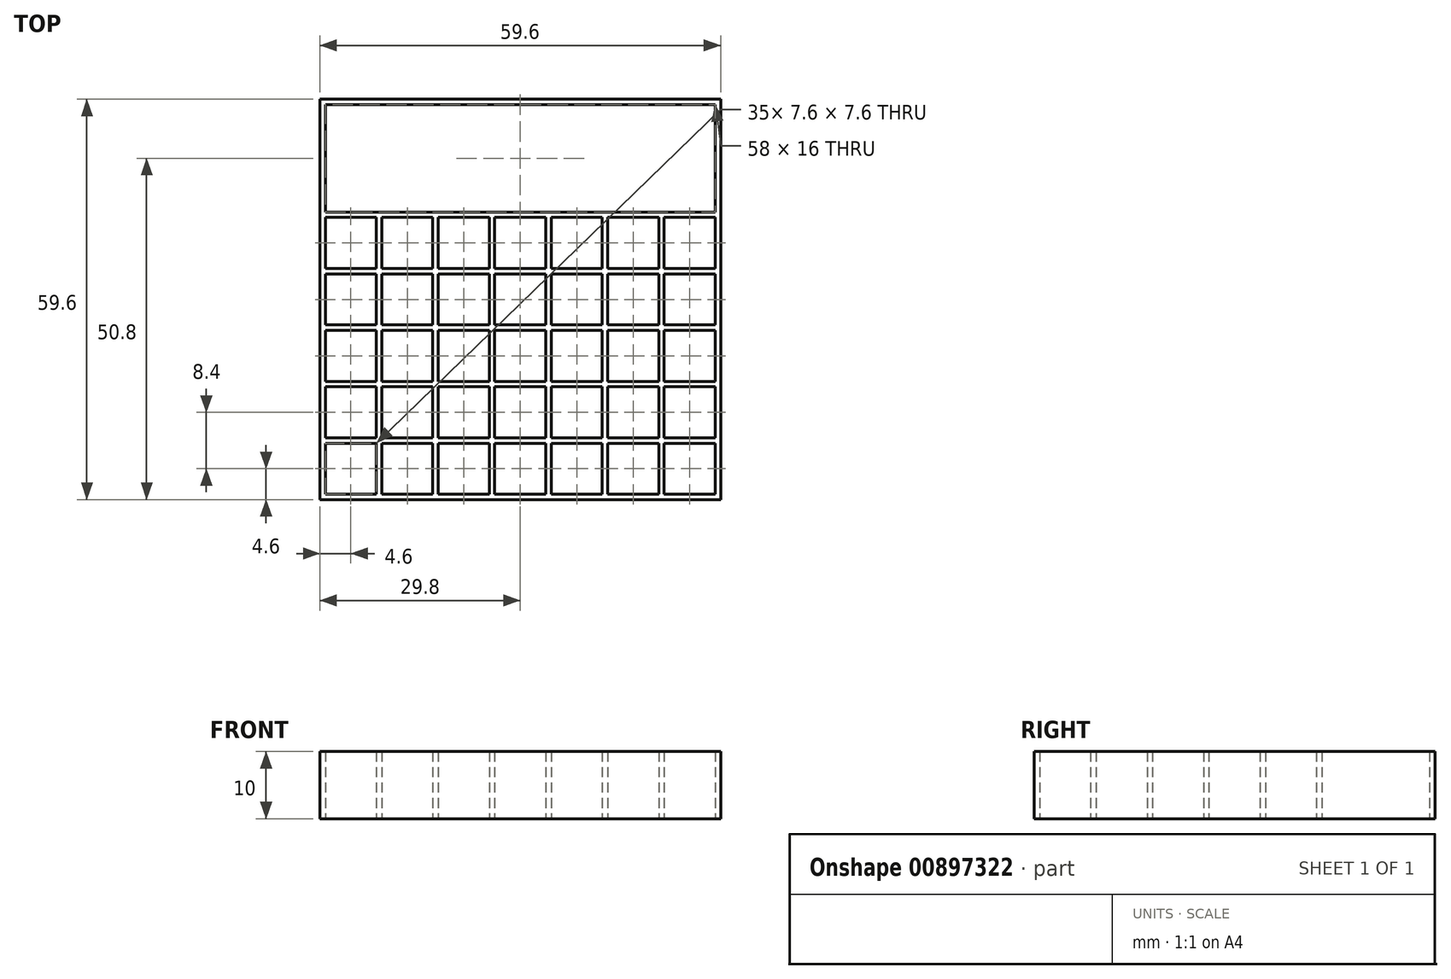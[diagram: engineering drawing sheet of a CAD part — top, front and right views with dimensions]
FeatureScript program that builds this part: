
annotation { "Feature Type Name" : "Feature", "Feature Type Description" : "" }
export const myFeature = defineFeature(function(context is Context, id is Id, definition is map)
    precondition{}
    {
        {
            var Q0;
            Q0=qCreatedBy(makeId("Top.planeOp"),FACE);
            var sketch = newSketch(context, id + "F0", { "sketchPlane" : qUnion([Q0])});
            skLineSegment(sketch, "E0.bottom", {"start": v(0, 29.8) * mm, "end": v(-29.8, 29.8) * mm});
            skLineSegment(sketch, "E1", {"start": v(-29.8, 29.8) * mm, "end": v(-29.8, 0) * mm});
            skLineSegment(sketch, "E2.2.0.1", {"start": v(-29, 12.2) * mm, "end": v(-21.4, 12.2) * mm});
            skLineSegment(sketch, "E2.2.0.4", {"start": v(-21.4, 12.2) * mm, "end": v(-21.4, 4.6) * mm});
            skLineSegment(sketch, "E2.2.0.7", {"start": v(-29, 12.2) * mm, "end": v(-29, 4.6) * mm});
            skLineSegment(sketch, "E2.2.0.15", {"start": v(-29, 4.6) * mm, "end": v(-21.4, 4.6) * mm});
            skLineSegment(sketch, "E3.MirrorCS", {"start": v(-29.8, -29.8) * mm, "end": v(-29.8, 0) * mm});
            skLineSegment(sketch, "E4.MirrorCS", {"start": v(0, -29.8) * mm, "end": v(-29.8, -29.8) * mm});
            skLineSegment(sketch, "E5", {"start": v(-29, 13) * mm, "end": v(0, 13) * mm});
            skLineSegment(sketch, "E6", {"start": v(-29, 13) * mm, "end": v(-29, 29) * mm});
            skLineSegment(sketch, "E7", {"start": v(-29, 29) * mm, "end": v(0, 29) * mm});
            skLineSegment(sketch, "E8.2.0.1", {"start": v(-20.6, 12.2) * mm, "end": v(-13, 12.2) * mm});
            skLineSegment(sketch, "E8.2.0.4", {"start": v(-13, 12.2) * mm, "end": v(-13, 4.6) * mm});
            skLineSegment(sketch, "E8.2.0.7", {"start": v(-20.6, 12.2) * mm, "end": v(-20.6, 4.6) * mm});
            skLineSegment(sketch, "E8.2.0.15", {"start": v(-20.6, 4.6) * mm, "end": v(-13, 4.6) * mm});
            skLineSegment(sketch, "E9.2.0.1", {"start": v(-12.2, 12.2) * mm, "end": v(-4.6, 12.2) * mm});
            skLineSegment(sketch, "E9.2.0.4", {"start": v(-4.6, 12.2) * mm, "end": v(-4.6, 4.6) * mm});
            skLineSegment(sketch, "E9.2.0.7", {"start": v(-12.2, 12.2) * mm, "end": v(-12.2, 4.6) * mm});
            skLineSegment(sketch, "E9.2.0.15", {"start": v(-12.2, 4.6) * mm, "end": v(-4.6, 4.6) * mm});
            skLineSegment(sketch, "E10.2.0.1", {"start": v(-3.8, 12.2) * mm, "end": v(0, 12.2) * mm});
            skLineSegment(sketch, "E10.2.0.7", {"start": v(-3.8, 12.2) * mm, "end": v(-3.8, 4.6) * mm});
            skLineSegment(sketch, "E10.2.0.15", {"start": v(-3.8, 4.6) * mm, "end": v(0, 4.6) * mm});
            skLineSegment(sketch, "E11.1.0.0", {"start": v(-20.6, 3.8) * mm, "end": v(-13, 3.8) * mm});
            skLineSegment(sketch, "E11.1.0.1", {"start": v(-29, -3.8) * mm, "end": v(-21.4, -3.8) * mm});
            skLineSegment(sketch, "E11.1.0.2", {"start": v(-21.4, 3.8) * mm, "end": v(-21.4, -3.8) * mm});
            skLineSegment(sketch, "E11.1.0.3", {"start": v(-12.2, 3.8) * mm, "end": v(-12.2, -3.8) * mm});
            skLineSegment(sketch, "E11.1.0.4", {"start": v(-4.6, 3.8) * mm, "end": v(-4.6, -3.8) * mm});
            skLineSegment(sketch, "E11.1.0.5", {"start": v(-29, 3.8) * mm, "end": v(-29, -3.8) * mm});
            skLineSegment(sketch, "E11.1.0.6", {"start": v(-3.8, -3.8) * mm, "end": v(0, -3.8) * mm});
            skLineSegment(sketch, "E11.1.0.7", {"start": v(-12.2, -3.8) * mm, "end": v(-4.6, -3.8) * mm});
            skLineSegment(sketch, "E11.1.0.8", {"start": v(-20.6, -3.8) * mm, "end": v(-13, -3.8) * mm});
            skLineSegment(sketch, "E11.1.0.9", {"start": v(-3.8, 3.8) * mm, "end": v(0, 3.8) * mm});
            skLineSegment(sketch, "E11.1.0.10", {"start": v(-20.6, 3.8) * mm, "end": v(-20.6, -3.8) * mm});
            skLineSegment(sketch, "E11.1.0.11", {"start": v(-29, 3.8) * mm, "end": v(-21.4, 3.8) * mm});
            skLineSegment(sketch, "E11.1.0.12", {"start": v(-12.2, 3.8) * mm, "end": v(-4.6, 3.8) * mm});
            skLineSegment(sketch, "E11.1.0.13", {"start": v(-3.8, 3.8) * mm, "end": v(-3.8, -3.8) * mm});
            skLineSegment(sketch, "E11.1.0.14", {"start": v(-13, 3.8) * mm, "end": v(-13, -3.8) * mm});
            skLineSegment(sketch, "E11.2.0.0", {"start": v(-20.6, -4.6) * mm, "end": v(-13, -4.6) * mm});
            skLineSegment(sketch, "E11.2.0.1", {"start": v(-29, -12.2) * mm, "end": v(-21.4, -12.2) * mm});
            skLineSegment(sketch, "E11.2.0.2", {"start": v(-21.4, -4.6) * mm, "end": v(-21.4, -12.2) * mm});
            skLineSegment(sketch, "E11.2.0.3", {"start": v(-12.2, -4.6) * mm, "end": v(-12.2, -12.2) * mm});
            skLineSegment(sketch, "E11.2.0.4", {"start": v(-4.6, -4.6) * mm, "end": v(-4.6, -12.2) * mm});
            skLineSegment(sketch, "E11.2.0.5", {"start": v(-29, -4.6) * mm, "end": v(-29, -12.2) * mm});
            skLineSegment(sketch, "E11.2.0.6", {"start": v(-3.8, -12.2) * mm, "end": v(0, -12.2) * mm});
            skLineSegment(sketch, "E11.2.0.7", {"start": v(-12.2, -12.2) * mm, "end": v(-4.6, -12.2) * mm});
            skLineSegment(sketch, "E11.2.0.8", {"start": v(-20.6, -12.2) * mm, "end": v(-13, -12.2) * mm});
            skLineSegment(sketch, "E11.2.0.9", {"start": v(-3.8, -4.6) * mm, "end": v(0, -4.6) * mm});
            skLineSegment(sketch, "E11.2.0.10", {"start": v(-20.6, -4.6) * mm, "end": v(-20.6, -12.2) * mm});
            skLineSegment(sketch, "E11.2.0.11", {"start": v(-29, -4.6) * mm, "end": v(-21.4, -4.6) * mm});
            skLineSegment(sketch, "E11.2.0.12", {"start": v(-12.2, -4.6) * mm, "end": v(-4.6, -4.6) * mm});
            skLineSegment(sketch, "E11.2.0.13", {"start": v(-3.8, -4.6) * mm, "end": v(-3.8, -12.2) * mm});
            skLineSegment(sketch, "E11.2.0.14", {"start": v(-13, -4.6) * mm, "end": v(-13, -12.2) * mm});
            skLineSegment(sketch, "E11.3.0.0", {"start": v(-20.6, -13) * mm, "end": v(-13, -13) * mm});
            skLineSegment(sketch, "E11.3.0.1", {"start": v(-29, -20.6) * mm, "end": v(-21.4, -20.6) * mm});
            skLineSegment(sketch, "E11.3.0.2", {"start": v(-21.4, -13) * mm, "end": v(-21.4, -20.6) * mm});
            skLineSegment(sketch, "E11.3.0.3", {"start": v(-12.2, -13) * mm, "end": v(-12.2, -20.6) * mm});
            skLineSegment(sketch, "E11.3.0.4", {"start": v(-4.6, -13) * mm, "end": v(-4.6, -20.6) * mm});
            skLineSegment(sketch, "E11.3.0.5", {"start": v(-29, -13) * mm, "end": v(-29, -20.6) * mm});
            skLineSegment(sketch, "E11.3.0.6", {"start": v(-3.8, -20.6) * mm, "end": v(0, -20.6) * mm});
            skLineSegment(sketch, "E11.3.0.7", {"start": v(-12.2, -20.6) * mm, "end": v(-4.6, -20.6) * mm});
            skLineSegment(sketch, "E11.3.0.8", {"start": v(-20.6, -20.6) * mm, "end": v(-13, -20.6) * mm});
            skLineSegment(sketch, "E11.3.0.9", {"start": v(-3.8, -13) * mm, "end": v(0, -13) * mm});
            skLineSegment(sketch, "E11.3.0.10", {"start": v(-20.6, -13) * mm, "end": v(-20.6, -20.6) * mm});
            skLineSegment(sketch, "E11.3.0.11", {"start": v(-29, -13) * mm, "end": v(-21.4, -13) * mm});
            skLineSegment(sketch, "E11.3.0.12", {"start": v(-12.2, -13) * mm, "end": v(-4.6, -13) * mm});
            skLineSegment(sketch, "E11.3.0.13", {"start": v(-3.8, -13) * mm, "end": v(-3.8, -20.6) * mm});
            skLineSegment(sketch, "E11.3.0.14", {"start": v(-13, -13) * mm, "end": v(-13, -20.6) * mm});
            skLineSegment(sketch, "E11.4.0.0", {"start": v(-20.6, -21.4) * mm, "end": v(-13, -21.4) * mm});
            skLineSegment(sketch, "E11.4.0.1", {"start": v(-29, -29) * mm, "end": v(-21.4, -29) * mm});
            skLineSegment(sketch, "E11.4.0.2", {"start": v(-21.4, -21.4) * mm, "end": v(-21.4, -29) * mm});
            skLineSegment(sketch, "E11.4.0.3", {"start": v(-12.2, -21.4) * mm, "end": v(-12.2, -29) * mm});
            skLineSegment(sketch, "E11.4.0.4", {"start": v(-4.6, -21.4) * mm, "end": v(-4.6, -29) * mm});
            skLineSegment(sketch, "E11.4.0.5", {"start": v(-29, -21.4) * mm, "end": v(-29, -29) * mm});
            skLineSegment(sketch, "E11.4.0.6", {"start": v(-3.8, -29) * mm, "end": v(0, -29) * mm});
            skLineSegment(sketch, "E11.4.0.7", {"start": v(-12.2, -29) * mm, "end": v(-4.6, -29) * mm});
            skLineSegment(sketch, "E11.4.0.8", {"start": v(-20.6, -29) * mm, "end": v(-13, -29) * mm});
            skLineSegment(sketch, "E11.4.0.9", {"start": v(-3.8, -21.4) * mm, "end": v(0, -21.4) * mm});
            skLineSegment(sketch, "E11.4.0.10", {"start": v(-20.6, -21.4) * mm, "end": v(-20.6, -29) * mm});
            skLineSegment(sketch, "E11.4.0.11", {"start": v(-29, -21.4) * mm, "end": v(-21.4, -21.4) * mm});
            skLineSegment(sketch, "E11.4.0.12", {"start": v(-12.2, -21.4) * mm, "end": v(-4.6, -21.4) * mm});
            skLineSegment(sketch, "E11.4.0.13", {"start": v(-3.8, -21.4) * mm, "end": v(-3.8, -29) * mm});
            skLineSegment(sketch, "E11.4.0.14", {"start": v(-13, -21.4) * mm, "end": v(-13, -29) * mm});
            skLineSegment(sketch, "E11.direction1", {"start": v(-29, 4.6) * mm, "end": v(-29, -3.8) * mm, "construction": true});
            skLineSegment(sketch, "E12.MirrorCS", {"start": v(3.8, 12.2) * mm, "end": v(3.8, 4.6) * mm});
            skLineSegment(sketch, "E13.MirrorCS", {"start": v(3.8, 12.2) * mm, "end": v(0, 12.2) * mm});
            skLineSegment(sketch, "E14.MirrorCS", {"start": v(12.2, 12.2) * mm, "end": v(12.2, 4.6) * mm});
            skLineSegment(sketch, "E15.MirrorCS", {"start": v(29, 3.8) * mm, "end": v(29, -3.8) * mm});
            skLineSegment(sketch, "E16.MirrorCS", {"start": v(20.6, 12.2) * mm, "end": v(20.6, 4.6) * mm});
            skLineSegment(sketch, "E17.MirrorCS", {"start": v(20.6, 3.8) * mm, "end": v(13, 3.8) * mm});
            skLineSegment(sketch, "E18.MirrorCS", {"start": v(29.8, -29.8) * mm, "end": v(29.8, 0) * mm});
            skLineSegment(sketch, "E19.MirrorCS", {"start": v(29.8, 29.8) * mm, "end": v(29.8, 0) * mm});
            skLineSegment(sketch, "E20.MirrorCS", {"start": v(20.6, -21.4) * mm, "end": v(20.6, -29) * mm});
            skLineSegment(sketch, "E21.MirrorCS", {"start": v(12.2, -4.6) * mm, "end": v(4.6, -4.6) * mm});
            skLineSegment(sketch, "E22.MirrorCS", {"start": v(20.6, -21.4) * mm, "end": v(13, -21.4) * mm});
            skLineSegment(sketch, "E23.MirrorCS", {"start": v(12.2, -13) * mm, "end": v(4.6, -13) * mm});
            skLineSegment(sketch, "E24.MirrorCS", {"start": v(12.2, 3.8) * mm, "end": v(12.2, -3.8) * mm});
            skLineSegment(sketch, "E25.MirrorCS", {"start": v(29, -21.4) * mm, "end": v(29, -29) * mm});
            skLineSegment(sketch, "E26.MirrorCS", {"start": v(20.6, -3.8) * mm, "end": v(13, -3.8) * mm});
            skLineSegment(sketch, "E27.MirrorCS", {"start": v(29, -4.6) * mm, "end": v(21.4, -4.6) * mm});
            skLineSegment(sketch, "E28.MirrorCS", {"start": v(21.4, -13) * mm, "end": v(21.4, -20.6) * mm});
            skLineSegment(sketch, "E29.MirrorCS", {"start": v(3.8, -13) * mm, "end": v(3.8, -20.6) * mm});
            skLineSegment(sketch, "E30.MirrorCS", {"start": v(29, 4.6) * mm, "end": v(21.4, 4.6) * mm});
            skLineSegment(sketch, "E31.MirrorCS", {"start": v(0, -29.8) * mm, "end": v(29.8, -29.8) * mm});
            skLineSegment(sketch, "E32.MirrorCS", {"start": v(20.6, -20.6) * mm, "end": v(13, -20.6) * mm});
            skLineSegment(sketch, "E33.MirrorCS", {"start": v(3.8, -12.2) * mm, "end": v(0, -12.2) * mm});
            skLineSegment(sketch, "E34.MirrorCS", {"start": v(12.2, -21.4) * mm, "end": v(4.6, -21.4) * mm});
            skLineSegment(sketch, "E35.MirrorCS", {"start": v(3.8, -13) * mm, "end": v(0, -13) * mm});
            skLineSegment(sketch, "E36.MirrorCS", {"start": v(4.6, -21.4) * mm, "end": v(4.6, -29) * mm});
            skLineSegment(sketch, "E37.MirrorCS", {"start": v(20.6, -29) * mm, "end": v(13, -29) * mm});
            skLineSegment(sketch, "E38.MirrorCS", {"start": v(20.6, 12.2) * mm, "end": v(13, 12.2) * mm});
            skLineSegment(sketch, "E39.MirrorCS", {"start": v(29, 13) * mm, "end": v(29, 29) * mm});
            skLineSegment(sketch, "E40.MirrorCS", {"start": v(13, -21.4) * mm, "end": v(13, -29) * mm});
            skLineSegment(sketch, "E41.MirrorCS", {"start": v(12.2, 4.6) * mm, "end": v(4.6, 4.6) * mm});
            skLineSegment(sketch, "E42.MirrorCS", {"start": v(29, -3.8) * mm, "end": v(21.4, -3.8) * mm});
            skLineSegment(sketch, "E43.MirrorCS", {"start": v(29, -21.4) * mm, "end": v(21.4, -21.4) * mm});
            skLineSegment(sketch, "E44.MirrorCS", {"start": v(20.6, -13) * mm, "end": v(13, -13) * mm});
            skLineSegment(sketch, "E45.MirrorCS", {"start": v(29, 3.8) * mm, "end": v(21.4, 3.8) * mm});
            skLineSegment(sketch, "E46.MirrorCS", {"start": v(29, -4.6) * mm, "end": v(29, -12.2) * mm});
            skLineSegment(sketch, "E47.MirrorCS", {"start": v(13, -4.6) * mm, "end": v(13, -12.2) * mm});
            skLineSegment(sketch, "E48.MirrorCS", {"start": v(3.8, -21.4) * mm, "end": v(0, -21.4) * mm});
            skLineSegment(sketch, "E49.MirrorCS", {"start": v(3.8, 3.8) * mm, "end": v(3.8, -3.8) * mm});
            skLineSegment(sketch, "E50.MirrorCS", {"start": v(20.6, -12.2) * mm, "end": v(13, -12.2) * mm});
            skLineSegment(sketch, "E51.MirrorCS", {"start": v(12.2, -3.8) * mm, "end": v(4.6, -3.8) * mm});
            skLineSegment(sketch, "E52.MirrorCS", {"start": v(21.4, -21.4) * mm, "end": v(21.4, -29) * mm});
            skLineSegment(sketch, "E53.MirrorCS", {"start": v(12.2, -20.6) * mm, "end": v(4.6, -20.6) * mm});
            skLineSegment(sketch, "E54.MirrorCS", {"start": v(13, 12.2) * mm, "end": v(13, 4.6) * mm});
            skLineSegment(sketch, "E55.MirrorCS", {"start": v(3.8, -4.6) * mm, "end": v(0, -4.6) * mm});
            skLineSegment(sketch, "E56.MirrorCS", {"start": v(12.2, 12.2) * mm, "end": v(4.6, 12.2) * mm});
            skLineSegment(sketch, "E57.MirrorCS", {"start": v(29, 12.2) * mm, "end": v(29, 4.6) * mm});
            skLineSegment(sketch, "E58.MirrorCS", {"start": v(12.2, -4.6) * mm, "end": v(12.2, -12.2) * mm});
            skLineSegment(sketch, "E59.MirrorCS", {"start": v(29, -12.2) * mm, "end": v(21.4, -12.2) * mm});
            skLineSegment(sketch, "E60.MirrorCS", {"start": v(13, -13) * mm, "end": v(13, -20.6) * mm});
            skLineSegment(sketch, "E61.MirrorCS", {"start": v(3.8, -21.4) * mm, "end": v(3.8, -29) * mm});
            skLineSegment(sketch, "E62.MirrorCS", {"start": v(12.2, -29) * mm, "end": v(4.6, -29) * mm});
            skLineSegment(sketch, "E63.MirrorCS", {"start": v(21.4, -4.6) * mm, "end": v(21.4, -12.2) * mm});
            skLineSegment(sketch, "E64.MirrorCS", {"start": v(0, 29.8) * mm, "end": v(29.8, 29.8) * mm});
            skLineSegment(sketch, "E65.MirrorCS", {"start": v(21.4, 3.8) * mm, "end": v(21.4, -3.8) * mm});
            skLineSegment(sketch, "E66.MirrorCS", {"start": v(29, 29) * mm, "end": v(0, 29) * mm});
            skLineSegment(sketch, "E67.MirrorCS", {"start": v(29, -13) * mm, "end": v(29, -20.6) * mm});
            skLineSegment(sketch, "E68.MirrorCS", {"start": v(20.6, -4.6) * mm, "end": v(13, -4.6) * mm});
            skLineSegment(sketch, "E69.MirrorCS", {"start": v(4.6, -4.6) * mm, "end": v(4.6, -12.2) * mm});
            skLineSegment(sketch, "E70.MirrorCS", {"start": v(29, -13) * mm, "end": v(21.4, -13) * mm});
            skLineSegment(sketch, "E71.MirrorCS", {"start": v(12.2, 3.8) * mm, "end": v(4.6, 3.8) * mm});
            skLineSegment(sketch, "E72.MirrorCS", {"start": v(3.8, 4.6) * mm, "end": v(0, 4.6) * mm});
            skLineSegment(sketch, "E73.MirrorCS", {"start": v(3.8, 3.8) * mm, "end": v(0, 3.8) * mm});
            skLineSegment(sketch, "E74.MirrorCS", {"start": v(29, 13) * mm, "end": v(0, 13) * mm});
            skLineSegment(sketch, "E75.MirrorCS", {"start": v(4.6, -13) * mm, "end": v(4.6, -20.6) * mm});
            skLineSegment(sketch, "E76.MirrorCS", {"start": v(3.8, -20.6) * mm, "end": v(0, -20.6) * mm});
            skLineSegment(sketch, "E77.MirrorCS", {"start": v(20.6, 4.6) * mm, "end": v(13, 4.6) * mm});
            skLineSegment(sketch, "E78.MirrorCS", {"start": v(12.2, -12.2) * mm, "end": v(4.6, -12.2) * mm});
            skLineSegment(sketch, "E79.MirrorCS", {"start": v(12.2, -21.4) * mm, "end": v(12.2, -29) * mm});
            skLineSegment(sketch, "E80.MirrorCS", {"start": v(20.6, -13) * mm, "end": v(20.6, -20.6) * mm});
            skLineSegment(sketch, "E81.MirrorCS", {"start": v(21.4, 12.2) * mm, "end": v(21.4, 4.6) * mm});
            skLineSegment(sketch, "E82.MirrorCS", {"start": v(4.6, 3.8) * mm, "end": v(4.6, -3.8) * mm});
            skLineSegment(sketch, "E83.MirrorCS", {"start": v(4.6, 12.2) * mm, "end": v(4.6, 4.6) * mm});
            skLineSegment(sketch, "E84.MirrorCS", {"start": v(3.8, -4.6) * mm, "end": v(3.8, -12.2) * mm});
            skLineSegment(sketch, "E85.MirrorCS", {"start": v(13, 3.8) * mm, "end": v(13, -3.8) * mm});
            skLineSegment(sketch, "E86.MirrorCS", {"start": v(20.6, -4.6) * mm, "end": v(20.6, -12.2) * mm});
            skLineSegment(sketch, "E87.MirrorCS", {"start": v(3.8, -3.8) * mm, "end": v(0, -3.8) * mm});
            skLineSegment(sketch, "E88.MirrorCS", {"start": v(20.6, 3.8) * mm, "end": v(20.6, -3.8) * mm});
            skLineSegment(sketch, "E89.MirrorCS", {"start": v(29, 4.6) * mm, "end": v(29, -3.8) * mm, "construction": true});
            skLineSegment(sketch, "E90.MirrorCS", {"start": v(29, -29) * mm, "end": v(21.4, -29) * mm});
            skLineSegment(sketch, "E91.MirrorCS", {"start": v(29, -20.6) * mm, "end": v(21.4, -20.6) * mm});
            skLineSegment(sketch, "E92.MirrorCS", {"start": v(12.2, -13) * mm, "end": v(12.2, -20.6) * mm});
            skLineSegment(sketch, "E93.MirrorCS", {"start": v(29, 12.2) * mm, "end": v(21.4, 12.2) * mm});
            skLineSegment(sketch, "E94.MirrorCS", {"start": v(3.8, -29) * mm, "end": v(0, -29) * mm});
            skSolve(sketch);
        }
        {
            var Q0;
            Q0=makeQuery(id+"F0.imprint","IMPRINT",FACE,{"disambiguationData":[TD([[makeQuery(id+"F0.imprint","IMPRINT",EDGE,{"derivedFrom":sQuery(id+"F0.wireOp",EDGE,"E0.bottom")}),1.0]])]});
            extrude(context, id + "F1", {"entities" : qUnion([Q0]), "depth" : 10 * mm, "offsetDistance" : 25 * mm});
        }
    });
